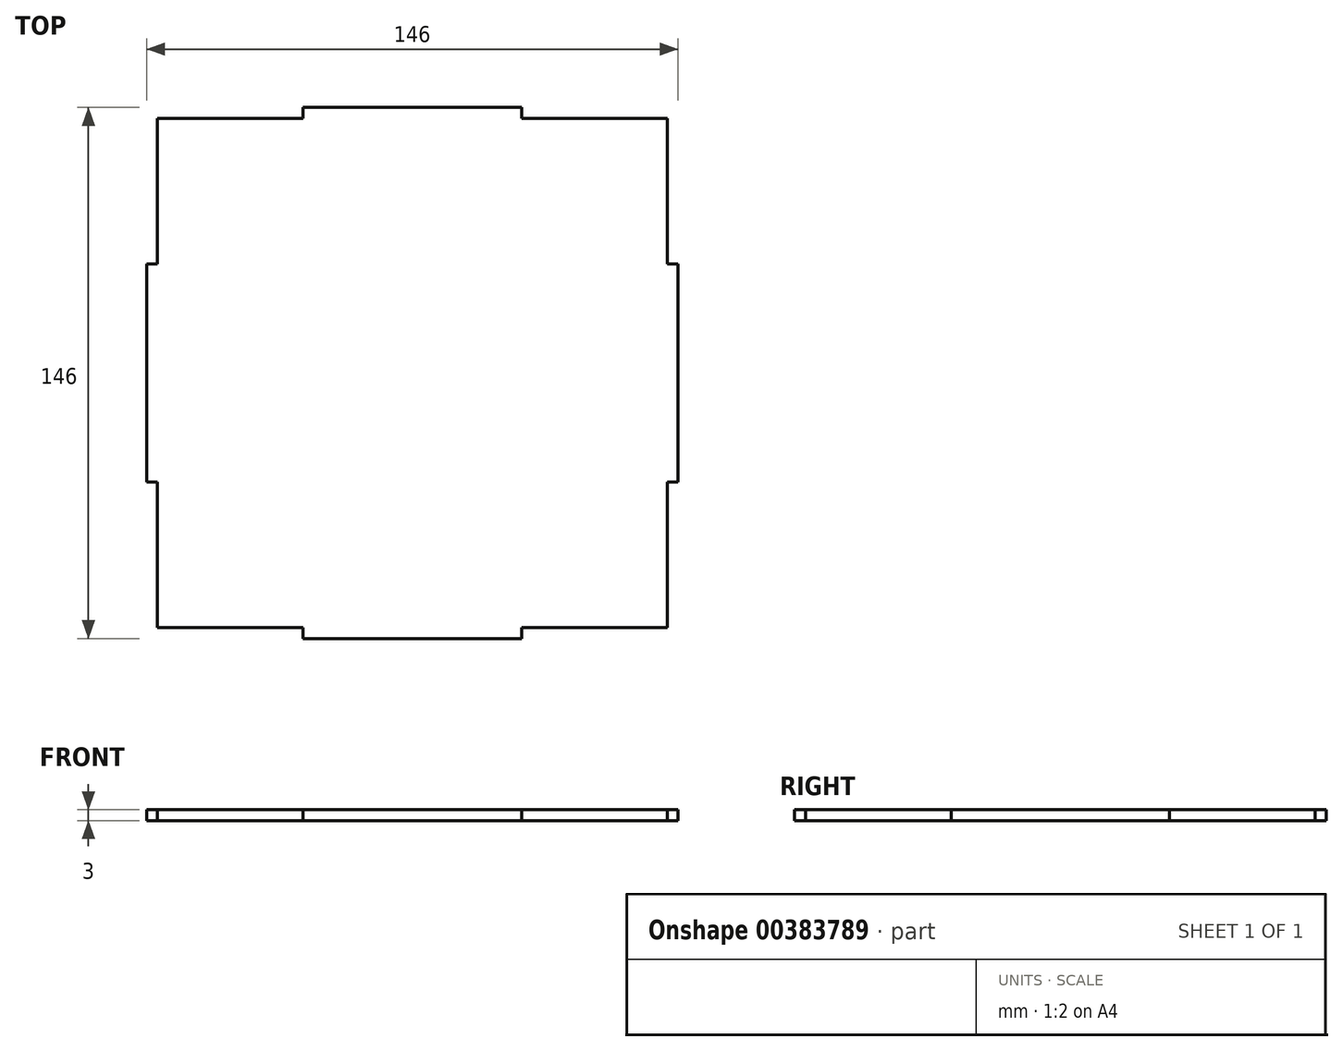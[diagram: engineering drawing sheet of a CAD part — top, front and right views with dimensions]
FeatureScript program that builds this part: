
annotation { "Feature Type Name" : "Feature", "Feature Type Description" : "" }
export const myFeature = defineFeature(function(context is Context, id is Id, definition is map)
    precondition{}
    {
        {
            var Q0;
            Q0=qCreatedBy(makeId("Top.planeOp"),FACE);
            var sketch = newSketch(context, id + "F0", { "sketchPlane" : qUnion([Q0])});
            skLineSegment(sketch, "E0.bottom", {"start": v(70, -70) * mm, "end": v(30, -70) * mm});
            skLineSegment(sketch, "E0.top", {"start": v(70, 70) * mm, "end": v(30, 70) * mm});
            skLineSegment(sketch, "E0.left", {"start": v(70, -70) * mm, "end": v(70, -30) * mm});
            skLineSegment(sketch, "E0.right", {"start": v(-70, -70) * mm, "end": v(-70, -30) * mm});
            skPoint(sketch, "E0.middle", {"position": v(0, 0) * mm});
            skLineSegment(sketch, "E1.top", {"start": v(30, 73) * mm, "end": v(-30, 73) * mm});
            skLineSegment(sketch, "E1.left", {"start": v(30, 70) * mm, "end": v(30, 73) * mm});
            skLineSegment(sketch, "E1.right", {"start": v(-30, 70) * mm, "end": v(-30, 73) * mm});
            skPoint(sketch, "E1.middle", {"position": v(0, 70) * mm});
            skPoint(sketch, "E1.bottom.end.orphan", {"position": v(-30, 67) * mm});
            skPoint(sketch, "E2.orphan", {"position": v(30, 67) * mm});
            skLineSegment(sketch, "E3.trimOffspring", {"start": v(-30, 70) * mm, "end": v(-70, 70) * mm});
            skLineSegment(sketch, "E4.bottom", {"start": v(73, -30) * mm, "end": v(70, -30) * mm});
            skLineSegment(sketch, "E4.top", {"start": v(73, 30) * mm, "end": v(70, 30) * mm});
            skLineSegment(sketch, "E4.left", {"start": v(73, -30) * mm, "end": v(73, 30) * mm});
            skPoint(sketch, "E4.middle", {"position": v(70, 0) * mm});
            skPoint(sketch, "E5.orphan", {"position": v(67, -30) * mm});
            skPoint(sketch, "E6.orphan", {"position": v(67, 30) * mm});
            skLineSegment(sketch, "E7.trimOffspring", {"start": v(70, 30) * mm, "end": v(70, 70) * mm});
            skPoint(sketch, "E8.middle", {"position": v(0, -70) * mm});
            skPoint(sketch, "E9.orphan", {"position": v(35.3, -67) * mm});
            skPoint(sketch, "E10.orphan", {"position": v(-24.7, -67) * mm});
            skLineSegment(sketch, "E11.trimOffspring", {"start": v(-30, -70) * mm, "end": v(-70, -70) * mm});
            skLineSegment(sketch, "E12.bottom", {"start": v(-73, -30) * mm, "end": v(-70, -30) * mm});
            skLineSegment(sketch, "E12.top", {"start": v(-73, 30) * mm, "end": v(-70, 30) * mm});
            skLineSegment(sketch, "E12.left", {"start": v(-73, -30) * mm, "end": v(-73, 30) * mm});
            skPoint(sketch, "E12.middle", {"position": v(-70, 0) * mm});
            skPoint(sketch, "E12.right.start.orphan", {"position": v(-67, -30) * mm});
            skPoint(sketch, "E13.orphan", {"position": v(-67, 30) * mm});
            skLineSegment(sketch, "E14.trimOffspring", {"start": v(-70, 30) * mm, "end": v(-70, 70) * mm});
            skLineSegment(sketch, "E15", {"start": v(-30, -70) * mm, "end": v(-30, -73) * mm});
            skLineSegment(sketch, "E16", {"start": v(-30, -73) * mm, "end": v(30, -73) * mm});
            skLineSegment(sketch, "E17", {"start": v(30, -70) * mm, "end": v(30, -73) * mm});
            skSolve(sketch);
        }
        {
            var Q0;
            Q0 = qSketchRegion(id + "F0", true);
            extrude(context, id + "F1", {"entities" : qUnion([Q0]), "depth" : 3 * mm});
        }
    });
